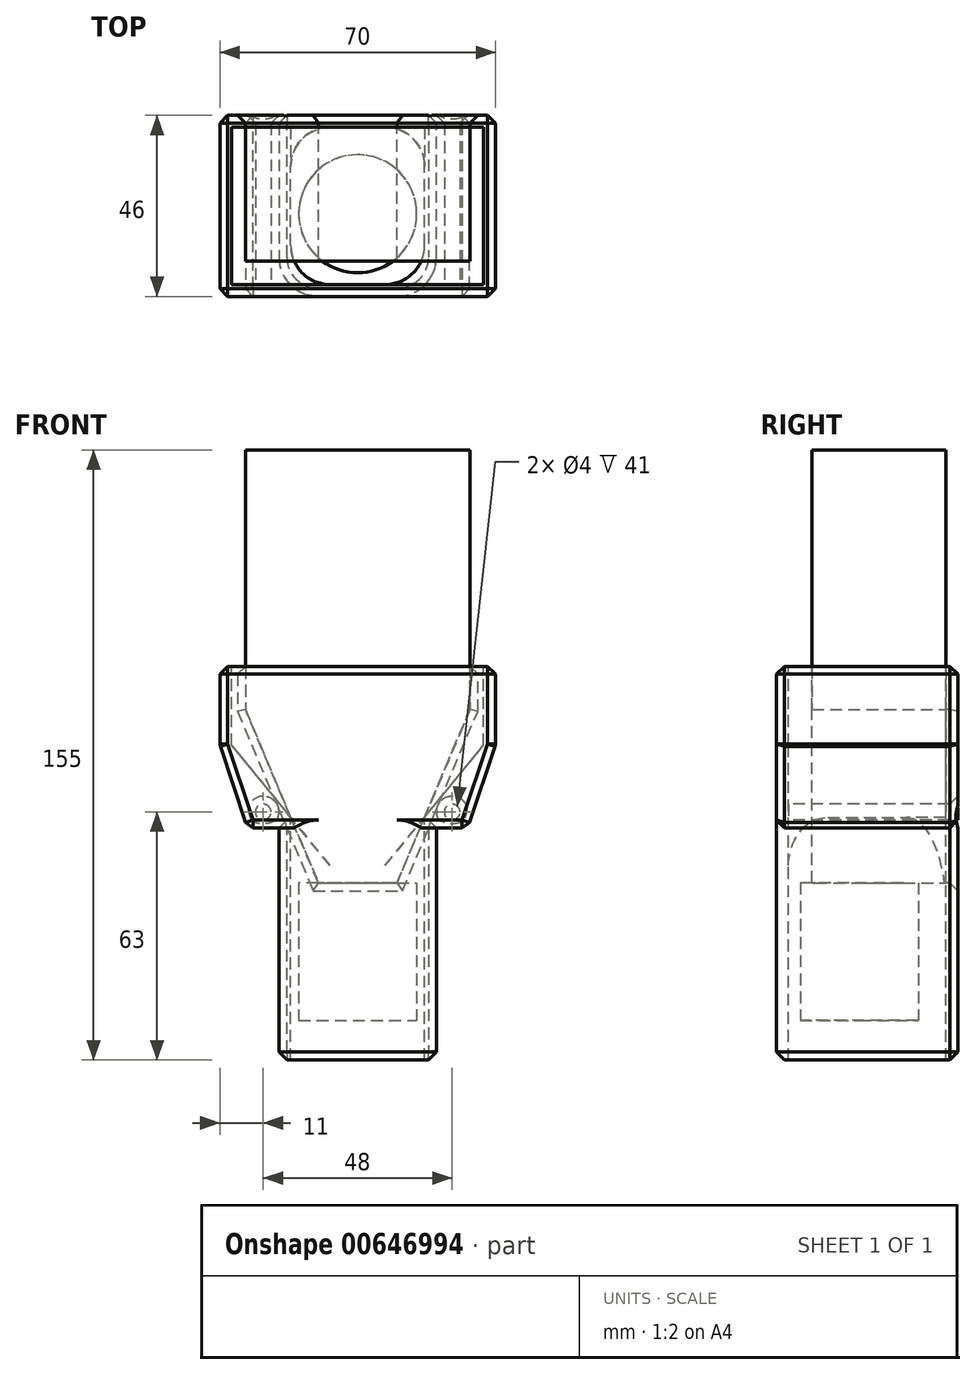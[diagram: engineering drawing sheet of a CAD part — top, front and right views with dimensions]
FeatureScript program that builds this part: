
annotation { "Feature Type Name" : "Feature", "Feature Type Description" : "" }
export const myFeature = defineFeature(function(context is Context, id is Id, definition is map)
    precondition{}
    {
        {
            var Q0;
            Q0=qCreatedBy(makeId("Front.planeOp"),FACE);
            var sketch = newSketch(context, id + "F0", { "sketchPlane" : qUnion([Q0])});
            skLineSegment(sketch, "E0", {"start": v(-10, 0) * mm, "end": v(10, 0) * mm});
            skLineSegment(sketch, "E1", {"start": v(10, 0) * mm, "end": v(28.5, 44) * mm});
            skLineSegment(sketch, "E2", {"start": v(28.5, 44) * mm, "end": v(28.5, 110) * mm});
            skLineSegment(sketch, "E3", {"start": v(28.5, 110) * mm, "end": v(-28.5, 110) * mm});
            skLineSegment(sketch, "E4", {"start": v(-28.5, 110) * mm, "end": v(-28.5, 44) * mm});
            skLineSegment(sketch, "E5", {"start": v(-28.5, 44) * mm, "end": v(-10, 0) * mm});
            skLineSegment(sketch, "E6.bottom", {"start": v(-15, 0) * mm, "end": v(15, 0) * mm});
            skLineSegment(sketch, "E6.top", {"start": v(-15, -35) * mm, "end": v(15, -35) * mm});
            skLineSegment(sketch, "E6.left", {"start": v(-15, 0) * mm, "end": v(-15, -35) * mm});
            skLineSegment(sketch, "E6.right", {"start": v(15, 0) * mm, "end": v(15, -35) * mm});
            skLineSegment(sketch, "E7", {"start": v(0, -35) * mm, "end": v(0, 0) * mm});
            skSolve(sketch);
        }
        {
            var Q0;
            {var subQ0=sQuery(id+"F0.wireOp",EDGE,"E1");Q0=makeQuery(id+"F0.imprint","IMPRINT",FACE,{"disambiguationData":[TD([[makeQuery(id+"F0.imprint","IMPRINT",EDGE,{"derivedFrom":subQ0}),1.0]])]});}
            extrude(context, id + "F1", {"entities" : qUnion([Q0]), "depth" : 12 * mm, "offsetDistance" : 25 * mm, "hasSecondDirection" : true, "secondDirectionOppositeDirection" : true, "secondDirectionDepth" : 22 * mm});
        }
        {
            var Q0;
            {var subQ0=sQuery(id+"F0.wireOp",EDGE,"E6.right");Q0=makeQuery(id+"F0.imprint","IMPRINT",FACE,{"disambiguationData":[TD([[makeQuery(id+"F0.imprint","IMPRINT",EDGE,{"derivedFrom":subQ0}),-1.0]])]});}
            var Q1;
            Q1=sQuery(id+"F0.wireOp",EDGE,"E7");
            revolve(context, id + "F2", {"operationType" : NewBodyOperationType.ADD, "entities" : qUnion([Q0]), "axis" : qUnion([Q1]), "revolveType" : RevolveType.FULL});
        }
        {
            var Q0;
            Q0=makeQuery(id+"F1.opExtrude","CAP_FACE",FACE,{"disambiguationData":[OSD([sQuery(id+"F0.wireOp",EDGE,"E1"),sQuery(id+"F0.wireOp",EDGE,"E2"),sQuery(id+"F0.wireOp",EDGE,"E3"),sQuery(id+"F0.wireOp",EDGE,"E4"),sQuery(id+"F0.wireOp",EDGE,"E5"),sQuery(id+"F0.wireOp",EDGE,"E6.bottom")])],"isStart":true});
            var sketch = newSketch(context, id + "F3", { "sketchPlane" : qUnion([Q0])});
            skLineSegment(sketch, "E8", {"start": v(35, 55) * mm, "end": v(-35, 55) * mm});
            skLineSegment(sketch, "E9", {"start": v(-35, 55) * mm, "end": v(-35, 35) * mm});
            skLineSegment(sketch, "E10", {"start": v(-20, 14) * mm, "end": v(-20, -45) * mm});
            skLineSegment(sketch, "E11", {"start": v(-20, -45) * mm, "end": v(20, -45) * mm});
            skLineSegment(sketch, "E12.MirrorCS", {"start": v(35, 55) * mm, "end": v(35, 35) * mm});
            skLineSegment(sketch, "E13.MirrorCS", {"start": v(20, 14) * mm, "end": v(20, -45) * mm});
            skCircle(sketch, "E14", {"center": v(-24, 18) * mm, "radius": 2 * mm});
            skCircle(sketch, "E15", {"center": v(24, 18) * mm, "radius": 2 * mm});
            skLineSegment(sketch, "E16", {"start": v(-17, -45) * mm, "end": v(-17, 16.65) * mm});
            skLineSegment(sketch, "E17", {"start": v(-17, 16.65) * mm, "end": v(-32, 35) * mm});
            skLineSegment(sketch, "E18", {"start": v(-32, 35) * mm, "end": v(-32, 55) * mm});
            skLineSegment(sketch, "E19.MirrorCS", {"start": v(32, 35) * mm, "end": v(32, 55) * mm});
            skLineSegment(sketch, "E20.MirrorCS", {"start": v(17, 16.65) * mm, "end": v(32, 35) * mm});
            skLineSegment(sketch, "E21.MirrorCS", {"start": v(17, -45) * mm, "end": v(17, 16.65) * mm});
            skLineSegment(sketch, "E22", {"start": v(-20, 14) * mm, "end": v(-28, 14) * mm});
            skLineSegment(sketch, "E23", {"start": v(-28, 14) * mm, "end": v(-35, 35) * mm});
            skLineSegment(sketch, "E24", {"start": v(20, 14) * mm, "end": v(28, 14) * mm});
            skLineSegment(sketch, "E25", {"start": v(28, 14) * mm, "end": v(35, 35) * mm});
            skSolve(sketch);
        }
        {
            var Q0;
            {var subQ3=sQuery(id+"F3.wireOp",EDGE,"E9");Q0=makeQuery(id+"F3.imprint","IMPRINT",FACE,{"disambiguationData":[TD([[makeQuery(id+"F3.imprint","IMPRINT",EDGE,{"derivedFrom":subQ3}),1.0]])]});}
            var Q1;
            {var subQ3=sQuery(id+"F3.wireOp",EDGE,"E17");Q1=makeQuery(id+"F3.imprint","IMPRINT",FACE,{"disambiguationData":[TD([[makeQuery(id+"F3.imprint","IMPRINT",EDGE,{"derivedFrom":subQ3}),-1.0]])]});}
            var Q2;
            {var subQ0=makeQuery(id+"F1.opExtrude","CAP_EDGE",EDGE,{"disambiguationData":[OSD([sQuery(id+"F0.wireOp",EDGE,"E6.bottom")])],"isStart":true});Q2=makeQuery(id+"F3.imprint","IMPRINT",FACE,{"disambiguationData":[TD([[makeQuery(id+"F3.imprint","IMPRINT",EDGE,{"derivedFrom":subQ0}),-1.0]])]});}
            var Q3;
            {var subQ1=sQuery(id+"F3.wireOp",EDGE,"E19.MirrorCS");Q3=makeQuery(id+"F3.imprint","IMPRINT",FACE,{"disambiguationData":[TD([[makeQuery(id+"F3.imprint","IMPRINT",EDGE,{"derivedFrom":subQ1}),1.0]])]});}
            var Q4;
            {var subQ1=sQuery(id+"F3.wireOp",EDGE,"E12.MirrorCS");Q4=makeQuery(id+"F3.imprint","IMPRINT",FACE,{"disambiguationData":[TD([[makeQuery(id+"F3.imprint","IMPRINT",EDGE,{"derivedFrom":subQ1}),-1.0]])]});}
            var Q5;
            {var subQ1=sQuery(id+"F3.wireOp",EDGE,"E16");Q5=makeQuery(id+"F3.imprint","IMPRINT",FACE,{"disambiguationData":[TD([[makeQuery(id+"F3.imprint","IMPRINT",EDGE,{"derivedFrom":subQ1}),-1.0]])]});}
            extrude(context, id + "F4", {"entities" : qUnion([Q0, Q1, Q2, Q3, Q4, Q5]), "depth" : 3 * mm, "offsetDistance" : 25 * mm});
        }
        {
            var Q0;
            {var subQ1=sQuery(id+"F3.wireOp",EDGE,"E12.MirrorCS");Q0=makeQuery(id+"F3.imprint","IMPRINT",FACE,{"disambiguationData":[TD([[makeQuery(id+"F3.imprint","IMPRINT",EDGE,{"derivedFrom":subQ1}),-1.0]])]});}
            var Q1;
            {var subQ3=sQuery(id+"F3.wireOp",EDGE,"E9");Q1=makeQuery(id+"F3.imprint","IMPRINT",FACE,{"disambiguationData":[TD([[makeQuery(id+"F3.imprint","IMPRINT",EDGE,{"derivedFrom":subQ3}),1.0]])]});}
            extrude(context, id + "F5", {"entities" : qUnion([Q0, Q1]), "operationType" : NewBodyOperationType.ADD, "oppositeDirection" : true, "depth" : 40 * mm, "offsetDistance" : 25 * mm});
        }
        {
            var Q0;
            Q0=makeQuery(id+"F5.opExtrude","CAP_FACE",FACE,{"disambiguationData":[OSD([sQuery(id+"F3.wireOp",EDGE,"E8"),sQuery(id+"F3.wireOp",EDGE,"E11"),sQuery(id+"F3.wireOp",EDGE,"E12.MirrorCS"),sQuery(id+"F3.wireOp",EDGE,"E13.MirrorCS"),sQuery(id+"F3.wireOp",EDGE,"E15"),sQuery(id+"F3.wireOp",EDGE,"E19.MirrorCS"),sQuery(id+"F3.wireOp",EDGE,"E20.MirrorCS"),sQuery(id+"F3.wireOp",EDGE,"E21.MirrorCS"),sQuery(id+"F3.wireOp",EDGE,"E24"),sQuery(id+"F3.wireOp",EDGE,"E25")])],"isStart":false});
            var sketch = newSketch(context, id + "F6", { "sketchPlane" : qUnion([Q0])});
            skLineSegment(sketch, "E26", {"start": v(35, 55) * mm, "end": v(-35, 55) * mm});
            skLineSegment(sketch, "E27", {"start": v(-20, -45) * mm, "end": v(20, -45) * mm});
            skLineSegment(sketch, "E28.MirrorCS", {"start": v(35, 55) * mm, "end": v(35, 35) * mm});
            skLineSegment(sketch, "E29.MirrorCS", {"start": v(20, 14) * mm, "end": v(20, -45) * mm});
            skLineSegment(sketch, "E30", {"start": v(20, 14) * mm, "end": v(28, 14) * mm});
            skLineSegment(sketch, "E31", {"start": v(28, 14) * mm, "end": v(35, 35) * mm});
            skLineSegment(sketch, "E32.MirrorCS", {"start": v(-35, 55) * mm, "end": v(-35, 35) * mm});
            skLineSegment(sketch, "E33.MirrorCS", {"start": v(-28, 14) * mm, "end": v(-35, 35) * mm});
            skLineSegment(sketch, "E34.MirrorCS", {"start": v(-20, 14) * mm, "end": v(-28, 14) * mm});
            skLineSegment(sketch, "E35.MirrorCS", {"start": v(-20, 14) * mm, "end": v(-20, -45) * mm});
            skSolve(sketch);
        }
        {
            var Q0;
            Q0 = qSketchRegion(id + "F6", true);
            extrude(context, id + "F7", {"entities" : qUnion([Q0]), "operationType" : NewBodyOperationType.ADD, "depth" : 3 * mm, "offsetDistance" : 25 * mm});
        }
        {
            var Q0;
            Q0=makeQuery(id+"F5.opExtrude","CAP_EDGE",EDGE,{"disambiguationData":[OSD([sQuery(id+"F3.wireOp",EDGE,"E21.MirrorCS")])],"isStart":true});
            var Q1;
            Q1=makeQuery(id+"F5.opExtrude","CAP_EDGE",EDGE,{"disambiguationData":[OSD([sQuery(id+"F3.wireOp",EDGE,"E16")])],"isStart":true});
            var Q2;
            Q2=makeQuery(id+"F5.opExtrude","CAP_EDGE",EDGE,{"disambiguationData":[OSD([sQuery(id+"F3.wireOp",EDGE,"E16")])],"isStart":false});
            var Q3;
            Q3=makeQuery(id+"F5.opExtrude","CAP_EDGE",EDGE,{"disambiguationData":[OSD([sQuery(id+"F3.wireOp",EDGE,"E21.MirrorCS")])],"isStart":false});
            var Q4;
            Q4=makeQuery(id+"F7.opExtrude","CAP_EDGE",EDGE,{"disambiguationData":[OSD([sQuery(id+"F6.wireOp",EDGE,"E35.MirrorCS")])],"isStart":false});
            var Q5;
            Q5=makeQuery(id+"F7.opExtrude","CAP_EDGE",EDGE,{"disambiguationData":[OSD([sQuery(id+"F6.wireOp",EDGE,"E29.MirrorCS")])],"isStart":false});
            fillet(context, id + "F8", {"entities" : qUnion([Q0, Q1, Q2, Q3, Q4, Q5]), "radius" : 10 * mm, "tangentPropagation" : true, "allowEdgeOverflow" : false});
        }
        {
            var Q0;
            Q0=makeQuery(id+"F4.opExtrude","CAP_FACE",FACE,{"disambiguationData":[OSD([sQuery(id+"F3.wireOp",EDGE,"E8"),sQuery(id+"F3.wireOp",EDGE,"E9"),sQuery(id+"F3.wireOp",EDGE,"E10"),sQuery(id+"F3.wireOp",EDGE,"E11"),sQuery(id+"F3.wireOp",EDGE,"E12.MirrorCS"),sQuery(id+"F3.wireOp",EDGE,"E13.MirrorCS"),sQuery(id+"F3.wireOp",EDGE,"E14"),sQuery(id+"F3.wireOp",EDGE,"E15"),sQuery(id+"F3.wireOp",EDGE,"E22"),sQuery(id+"F3.wireOp",EDGE,"E23"),sQuery(id+"F3.wireOp",EDGE,"E24"),sQuery(id+"F3.wireOp",EDGE,"E25")])],"isStart":false});
            var Q1;
            Q1=makeQuery(id+"F7.opExtrude","CAP_FACE",FACE,{"disambiguationData":[OSD([sQuery(id+"F6.wireOp",EDGE,"E26"),sQuery(id+"F6.wireOp",EDGE,"E27"),sQuery(id+"F6.wireOp",EDGE,"E28.MirrorCS"),sQuery(id+"F6.wireOp",EDGE,"E29.MirrorCS"),sQuery(id+"F6.wireOp",EDGE,"E30"),sQuery(id+"F6.wireOp",EDGE,"E31"),sQuery(id+"F6.wireOp",EDGE,"E32.MirrorCS"),sQuery(id+"F6.wireOp",EDGE,"E33.MirrorCS"),sQuery(id+"F6.wireOp",EDGE,"E34.MirrorCS"),sQuery(id+"F6.wireOp",EDGE,"E35.MirrorCS")])],"isStart":false});
            var Q2;
            {var subQ0=sQuery(id+"F3.wireOp",EDGE,"E25");Q2=makeQuery(id+"F7.boolean.opBoolean","MERGE",FACE,{"derivedFrom":[makeQuery(id+"F5.boolean.opBoolean","MERGE",FACE,{"derivedFrom":[makeQuery(id+"F4.opExtrude","SWEPT_FACE",FACE,{"disambiguationData":[OSD([subQ0])]}),makeQuery(id+"F5.opExtrude","SWEPT_FACE",FACE,{"disambiguationData":[OSD([subQ0])]})]}),makeQuery(id+"F7.opExtrude","SWEPT_FACE",FACE,{"disambiguationData":[OSD([sQuery(id+"F6.wireOp",EDGE,"E33.MirrorCS")])]})]});}
            var Q3;
            {var subQ0=sQuery(id+"F3.wireOp",EDGE,"E23");Q3=makeQuery(id+"F7.boolean.opBoolean","MERGE",FACE,{"derivedFrom":[makeQuery(id+"F5.boolean.opBoolean","MERGE",FACE,{"derivedFrom":[makeQuery(id+"F4.opExtrude","SWEPT_FACE",FACE,{"disambiguationData":[OSD([subQ0])]}),makeQuery(id+"F5.opExtrude","SWEPT_FACE",FACE,{"disambiguationData":[OSD([subQ0])]})]}),makeQuery(id+"F7.opExtrude","SWEPT_FACE",FACE,{"disambiguationData":[OSD([sQuery(id+"F6.wireOp",EDGE,"E31")])]})]});}
            var Q4;
            {var subQ0=sQuery(id+"F3.wireOp",EDGE,"E9");Q4=makeQuery(id+"F7.boolean.opBoolean","MERGE",FACE,{"derivedFrom":[makeQuery(id+"F5.boolean.opBoolean","MERGE",FACE,{"derivedFrom":[makeQuery(id+"F4.opExtrude","SWEPT_FACE",FACE,{"disambiguationData":[OSD([subQ0])]}),makeQuery(id+"F5.opExtrude","SWEPT_FACE",FACE,{"disambiguationData":[OSD([subQ0])]})]}),makeQuery(id+"F7.opExtrude","SWEPT_FACE",FACE,{"disambiguationData":[OSD([sQuery(id+"F6.wireOp",EDGE,"E28.MirrorCS")])]})]});}
            var Q5;
            {var subQ0=sQuery(id+"F3.wireOp",EDGE,"E12.MirrorCS");Q5=makeQuery(id+"F7.boolean.opBoolean","MERGE",FACE,{"derivedFrom":[makeQuery(id+"F5.boolean.opBoolean","MERGE",FACE,{"derivedFrom":[makeQuery(id+"F4.opExtrude","SWEPT_FACE",FACE,{"disambiguationData":[OSD([subQ0])]}),makeQuery(id+"F5.opExtrude","SWEPT_FACE",FACE,{"disambiguationData":[OSD([subQ0])]})]}),makeQuery(id+"F7.opExtrude","SWEPT_FACE",FACE,{"disambiguationData":[OSD([sQuery(id+"F6.wireOp",EDGE,"E32.MirrorCS")])]})]});}
            chamfer(context, id + "F9", {"entities" : qUnion([Q0, Q1, Q2, Q3, Q4, Q5]), "width" : 2 * mm, "tangentPropagation" : true});
        }
    });
